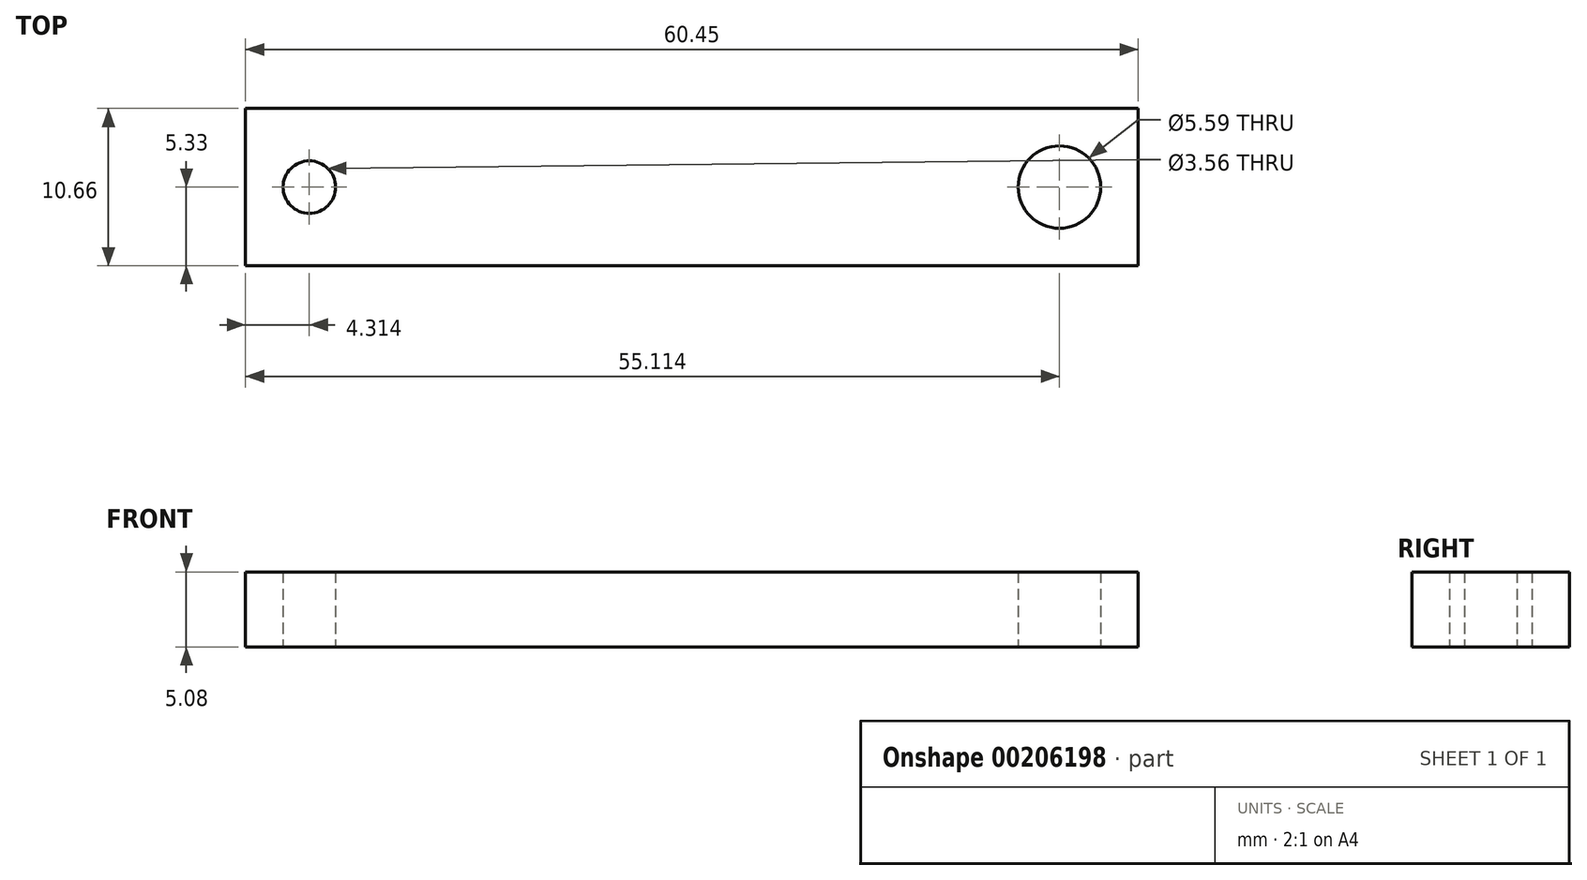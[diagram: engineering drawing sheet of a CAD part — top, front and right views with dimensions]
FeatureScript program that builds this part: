
annotation { "Feature Type Name" : "Feature", "Feature Type Description" : "" }
export const myFeature = defineFeature(function(context is Context, id is Id, definition is map)
    precondition{}
    {
        {
            var Q0;
            Q0=qCreatedBy(makeId("Top.planeOp"),FACE);
            var sketch = newSketch(context, id + "F0", { "sketchPlane" : qUnion([Q0])});
            skCircle(sketch, "E0", {"center": v(33.97, 0) * mm, "radius": 2.8 * mm});
            skLineSegment(sketch, "E1.bottom", {"start": v(39.3, -5.33) * mm, "end": v(-21.14, -5.33) * mm});
            skLineSegment(sketch, "E1.top", {"start": v(39.3, 5.33) * mm, "end": v(-21.14, 5.33) * mm});
            skLineSegment(sketch, "E1.left", {"start": v(39.3, -5.33) * mm, "end": v(39.3, 5.33) * mm});
            skLineSegment(sketch, "E1.right", {"start": v(-21.14, -5.33) * mm, "end": v(-21.14, 5.33) * mm});
            skCircle(sketch, "E2", {"center": v(-16.83, 0) * mm, "radius": 1.78 * mm});
            skSolve(sketch);
        }
        {
            var Q0;
            Q0 = qSketchRegion(id + "F0", true);
            extrude(context, id + "F1", {"entities" : qUnion([Q0]), "depth" : 5.08 * mm});
        }
    });
